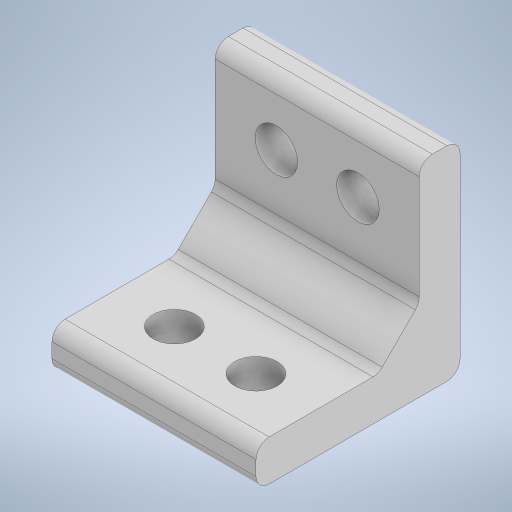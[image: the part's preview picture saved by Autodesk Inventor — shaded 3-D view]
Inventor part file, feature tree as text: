
AUTODESK INVENTOR PART (.ipt)
format: ipt  version: 2024.2 (Build 282272000, 272)  size: 274,944 bytes
history: native  units: mm
features: extrude x4, sketch x3, projected_geometry x2, other x1, chamfer x1, fillet x1
ambient origin geometry x8: Origin, YZ Plane, XZ Plane, XY Plane, X Axis, Y Axis, Z Axis, Center Point
bodies: Body1 (feature_tree)
feature tree (12):
  other  "Bryła1"
  sketch  "Szkic1"
  extrude  "Wyciągnięcie proste1"  Depth=5.0mm
  extrude  "Wyciągnięcie proste2"  Depth=25.0mm
  chamfer  "Faza1"  Distance=20.0mm
  extrude  "Wyciągnięcie proste3"  Depth=5.0mm TaperAngle=0.0deg
  extrude  "Wyciągnięcie proste4"  Depth=25.0mm TaperAngle=0.0deg
  fillet  "Zaokrąglenie1"  Radius=5.0mm
  sketch  "Szkic2"
  projected_geometry  "Pętla rzutowana1"
  sketch  "Szkic3"
  projected_geometry  "Pętla rzutowana2"
